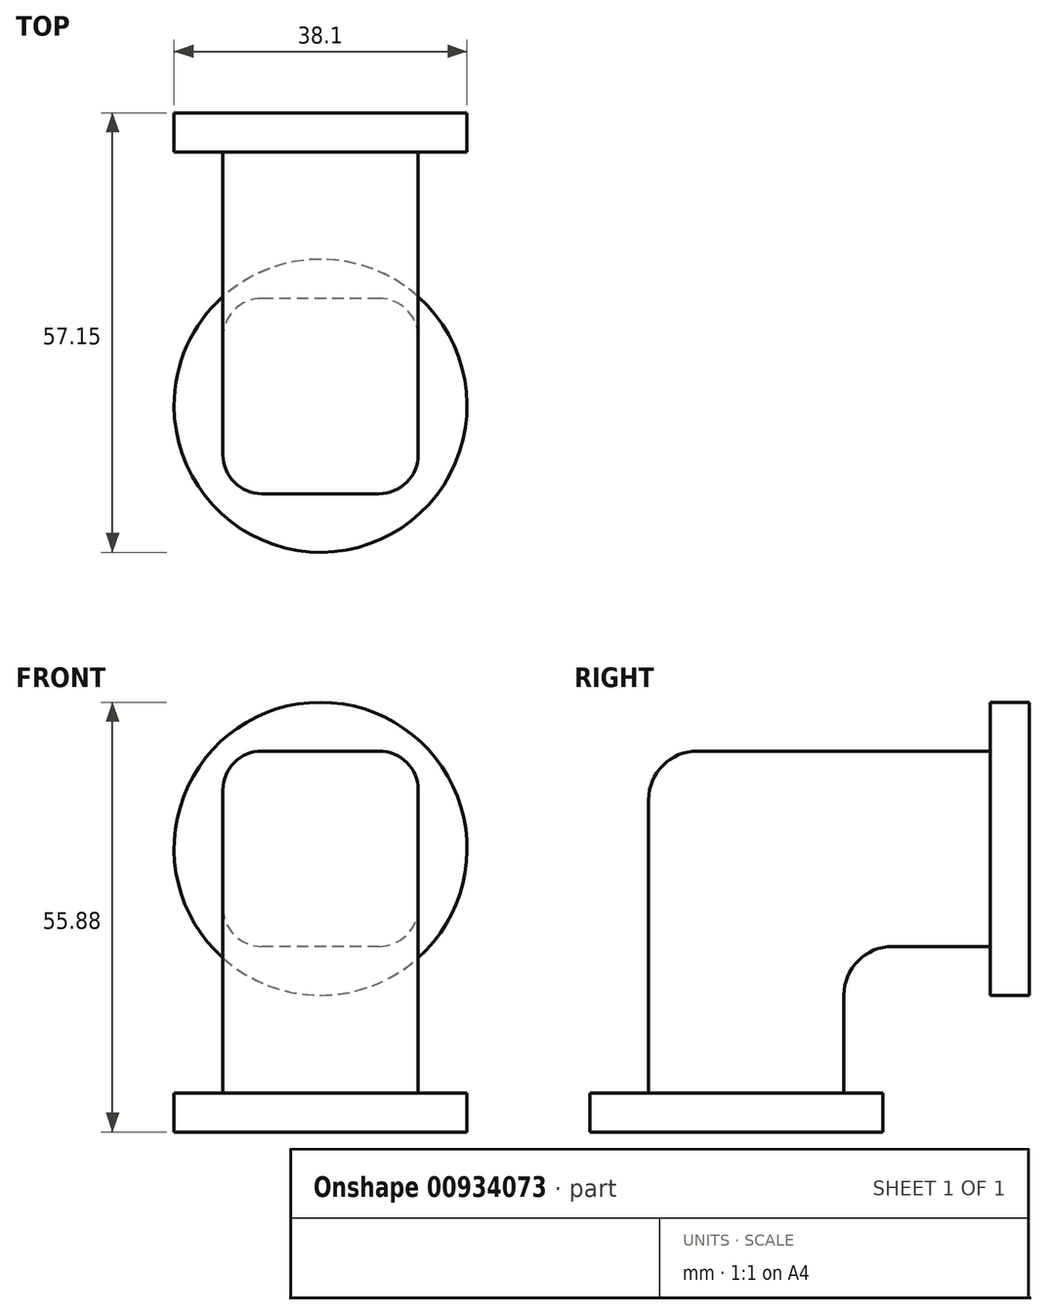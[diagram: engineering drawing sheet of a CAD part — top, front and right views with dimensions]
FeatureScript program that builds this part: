
annotation { "Feature Type Name" : "Feature", "Feature Type Description" : "" }
export const myFeature = defineFeature(function(context is Context, id is Id, definition is map)
    precondition{}
    {
        {
            var Q0;
            Q0=qCreatedBy(makeId("Front.planeOp"),FACE);
            var sketch = newSketch(context, id + "F0", { "sketchPlane" : qUnion([Q0])});
            skCircle(sketch, "E0", {"center": v(0, 0) * mm, "radius": 19.05 * mm});
            skSolve(sketch);
        }
        {
            var Q0;
            Q0 = qSketchRegion(id + "F0", true);
            extrude(context, id + "F1", {"entities" : qUnion([Q0]), "depth" : 5.08 * mm, "offsetDistance" : 25.4 * mm});
        }
        {
            var Q0;
            Q0=qCreatedBy(makeId("Right.planeOp"),FACE);
            var sketch = newSketch(context, id + "F2", { "sketchPlane" : qUnion([Q0])});
            skLineSegment(sketch, "E1.bottom", {"start": v(-5.08, 12.7) * mm, "end": v(-43.18, 12.7) * mm});
            skLineSegment(sketch, "E1.top", {"start": v(-5.08, -12.7) * mm, "end": v(-17.78, -12.7) * mm});
            skLineSegment(sketch, "E1.left", {"start": v(-5.08, 12.7) * mm, "end": v(-5.08, -12.7) * mm});
            skLineSegment(sketch, "E1.right", {"start": v(-49.53, 6.35) * mm, "end": v(-49.53, -12.7) * mm});
            skLineSegment(sketch, "E2.bottom", {"start": v(-24.13, -31.75) * mm, "end": v(-49.53, -31.75) * mm});
            skLineSegment(sketch, "E2.left", {"start": v(-24.13, -31.75) * mm, "end": v(-24.13, -19.05) * mm});
            skLineSegment(sketch, "E2.right", {"start": v(-49.53, -31.75) * mm, "end": v(-49.53, -12.7) * mm});
            skPoint(sketch, "E3.visualSharp", {"position": v(-49.53, 12.7) * mm});
            skArc(sketch, "E3.filletArc", {"start": v(-43.18, 12.7) * mm, "mid": v(-47.67, 10.84) * mm, "end": v(-49.53, 6.35) * mm});
            skPoint(sketch, "E4.visualSharp", {"position": v(-24.13, -12.7) * mm});
            skArc(sketch, "E4.filletArc", {"start": v(-17.78, -12.7) * mm, "mid": v(-22.27, -14.56) * mm, "end": v(-24.13, -19.05) * mm});
            skSolve(sketch);
        }
        {
            var Q0;
            Q0 = qSketchRegion(id + "F2", true);
            extrude(context, id + "F3", {"entities" : qUnion([Q0]), "operationType" : NewBodyOperationType.ADD, "endBound" : BoundingType.SYMMETRIC, "depth" : 25.4 * mm, "offsetDistance" : 25.4 * mm});
        }
        {
            var Q0;
            Q0=makeQuery(id+"F3.opExtrude","CAP_EDGE",EDGE,{"disambiguationData":[OSD([sQuery(id+"F2.wireOp",EDGE,"E1.bottom")])],"isStart":true});
            var Q1;
            Q1=makeQuery(id+"F3.opExtrude","CAP_EDGE",EDGE,{"disambiguationData":[OSD([sQuery(id+"F2.wireOp",EDGE,"E1.bottom")])],"isStart":false});
            var Q2;
            Q2=makeQuery(id+"F3.opExtrude","CAP_EDGE",EDGE,{"disambiguationData":[OSD([sQuery(id+"F2.wireOp",EDGE,"E1.top")])],"isStart":false});
            var Q3;
            Q3=makeQuery(id+"F3.opExtrude","CAP_EDGE",EDGE,{"disambiguationData":[OSD([sQuery(id+"F2.wireOp",EDGE,"E2.left")])],"isStart":true});
            fillet(context, id + "F4", {"entities" : qUnion([Q0, Q1, Q2, Q3]), "radius" : 5.08 * mm, "tangentPropagation" : true, "allowEdgeOverflow" : false});
        }
        {
            var Q0;
            Q0=makeQuery(id+"F3.opExtrude","SWEPT_FACE",FACE,{"disambiguationData":[OSD([sQuery(id+"F2.wireOp",EDGE,"E2.bottom")])]});
            var sketch = newSketch(context, id + "F5", { "sketchPlane" : qUnion([Q0])});
            skCircle(sketch, "E5", {"center": v(0, 38.1) * mm, "radius": 19.05 * mm});
            skSolve(sketch);
        }
        {
            var Q0;
            Q0 = qSketchRegion(id + "F5", true);
            extrude(context, id + "F6", {"entities" : qUnion([Q0]), "operationType" : NewBodyOperationType.ADD, "depth" : 5.08 * mm, "offsetDistance" : 25.4 * mm});
        }
    });
